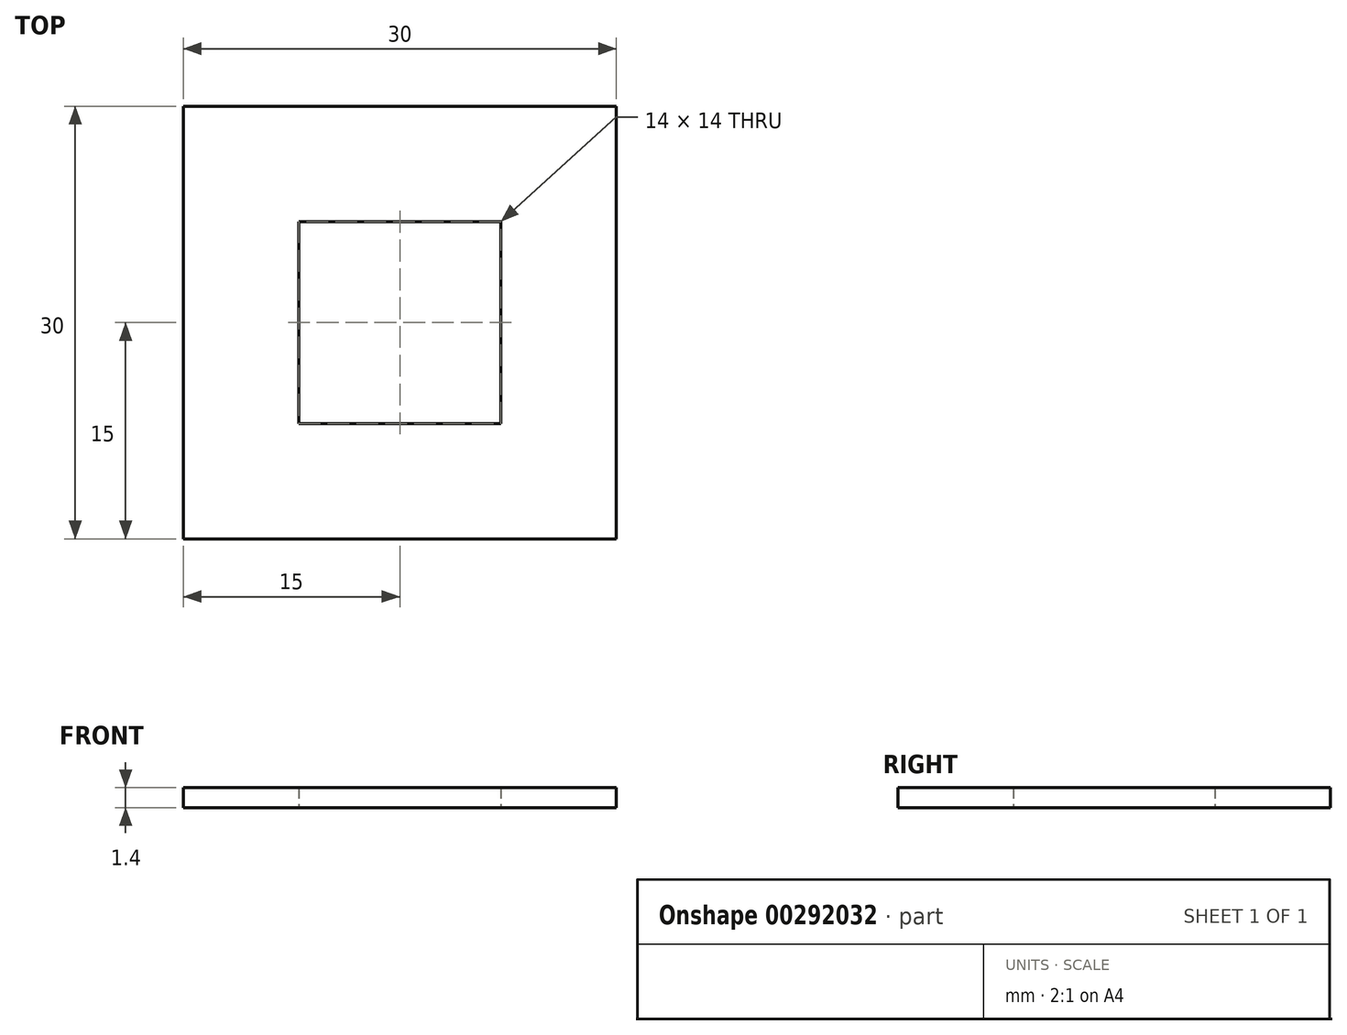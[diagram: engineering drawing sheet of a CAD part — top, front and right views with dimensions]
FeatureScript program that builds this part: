
annotation { "Feature Type Name" : "Feature", "Feature Type Description" : "" }
export const myFeature = defineFeature(function(context is Context, id is Id, definition is map)
    precondition{}
    {
        {
            var Q0;
            Q0=qCreatedBy(makeId("Top.planeOp"),FACE);
            var sketch = newSketch(context, id + "F0", { "sketchPlane" : qUnion([Q0])});
            skLineSegment(sketch, "E0.bottom", {"start": v(-7, 7) * mm, "end": v(7, 7) * mm});
            skLineSegment(sketch, "E0.top", {"start": v(-7, -7) * mm, "end": v(7, -7) * mm});
            skLineSegment(sketch, "E0.left", {"start": v(-7, 7) * mm, "end": v(-7, -7) * mm});
            skLineSegment(sketch, "E0.right", {"start": v(7, 7) * mm, "end": v(7, -7) * mm});
            skLineSegment(sketch, "E1.bottom", {"start": v(-15, 15) * mm, "end": v(15, 15) * mm});
            skLineSegment(sketch, "E1.top", {"start": v(-15, -15) * mm, "end": v(15, -15) * mm});
            skLineSegment(sketch, "E1.left", {"start": v(-15, 15) * mm, "end": v(-15, -15) * mm});
            skLineSegment(sketch, "E1.right", {"start": v(15, 15) * mm, "end": v(15, -15) * mm});
            skSolve(sketch);
        }
        {
            var Q0;
            Q0 = qSketchRegion(id + "F0", true);
            var Q1;
            Q1=makeQuery(id+"F0.imprint","IMPRINT",FACE,{"disambiguationData":[TD([[makeQuery(id+"F0.imprint","IMPRINT",EDGE,{"derivedFrom":sQuery(id+"F0.wireOp",EDGE,"E0.bottom")}),1.0]])]});
            extrude(context, id + "F1", {"entities" : qUnion([Q0, Q1]), "depth" : 1.4 * mm});
        }
    });
